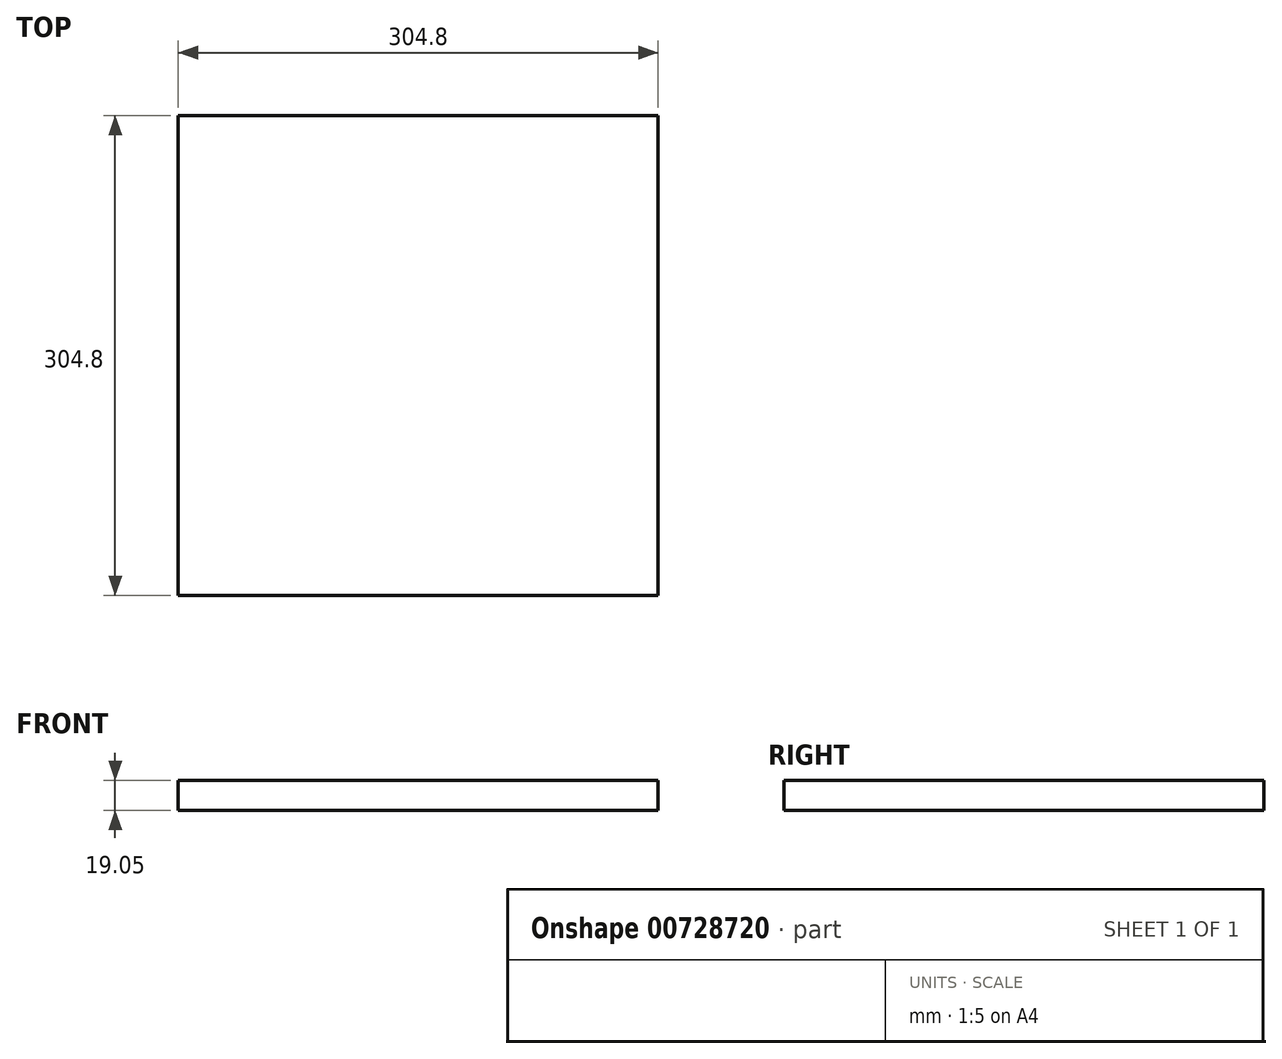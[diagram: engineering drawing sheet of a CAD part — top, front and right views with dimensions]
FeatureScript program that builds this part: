
annotation { "Feature Type Name" : "Feature", "Feature Type Description" : "" }
export const myFeature = defineFeature(function(context is Context, id is Id, definition is map)
    precondition{}
    {
        {
            var Q0;
            Q0=qCreatedBy(makeId("Top.planeOp"),FACE);
            var sketch = newSketch(context, id + "F0", { "sketchPlane" : qUnion([Q0])});
            skLineSegment(sketch, "E0.bottom", {"start": v(152.4, 152.4) * mm, "end": v(-152.4, 152.4) * mm});
            skLineSegment(sketch, "E0.top", {"start": v(152.4, -152.4) * mm, "end": v(-152.4, -152.4) * mm});
            skLineSegment(sketch, "E0.left", {"start": v(152.4, 152.4) * mm, "end": v(152.4, -152.4) * mm});
            skLineSegment(sketch, "E0.right", {"start": v(-152.4, 152.4) * mm, "end": v(-152.4, -152.4) * mm});
            skPoint(sketch, "E0.middle", {"position": v(0, 0) * mm});
            skSolve(sketch);
        }
        {
            var Q0;
            Q0 = qSketchRegion(id + "F0", true);
            extrude(context, id + "F1", {"entities" : qUnion([Q0]), "depth" : 19.05 * mm, "offsetDistance" : 25.4 * mm});
        }
    });
